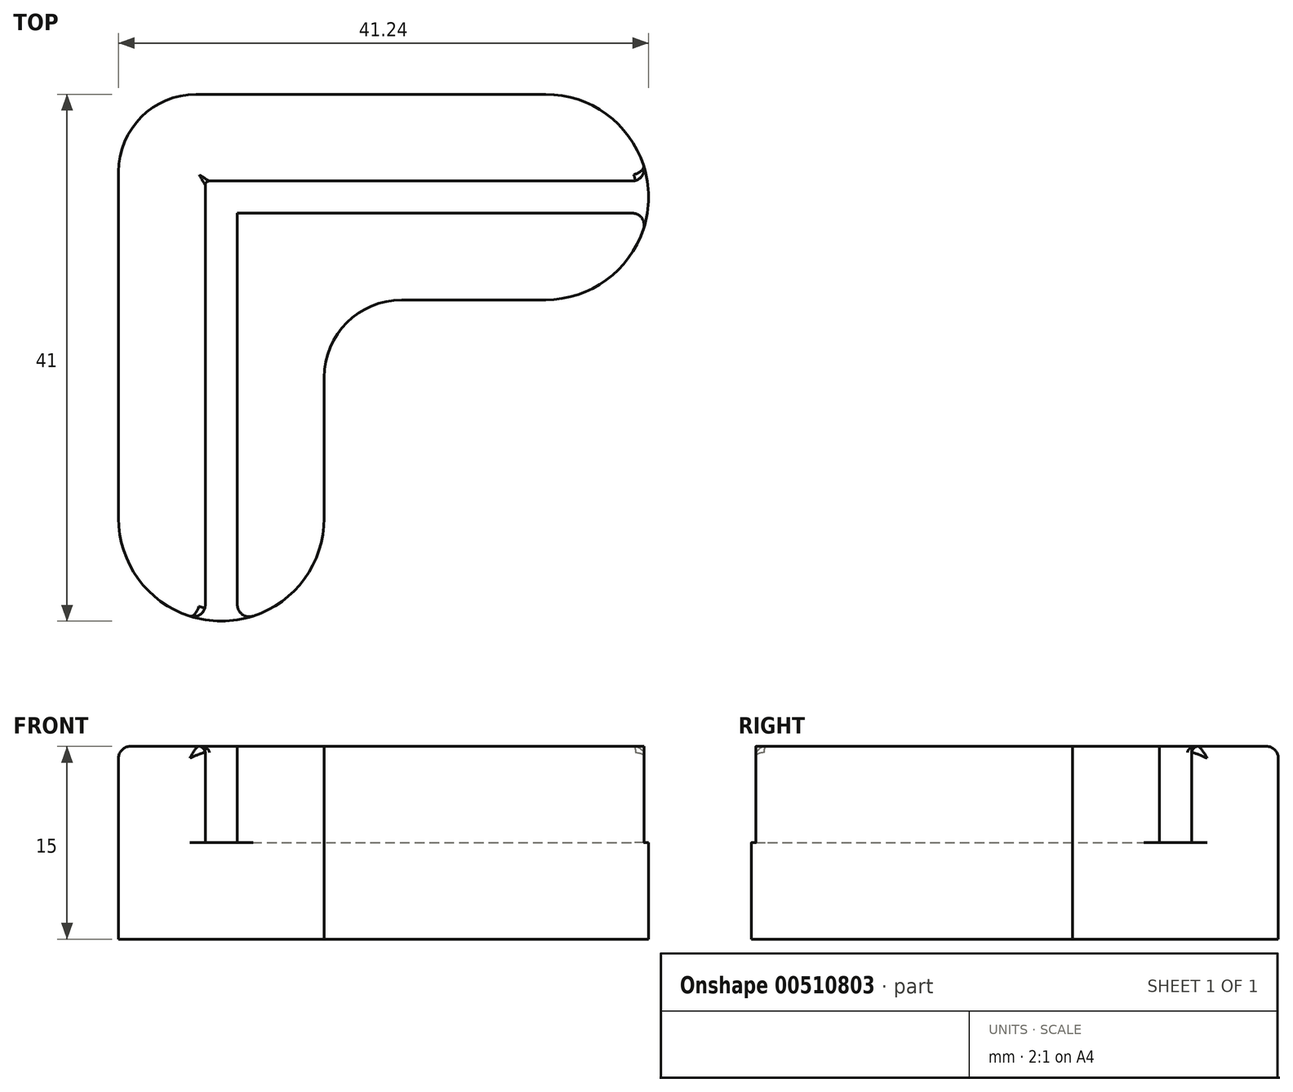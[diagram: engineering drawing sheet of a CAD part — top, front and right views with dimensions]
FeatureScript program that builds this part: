
annotation { "Feature Type Name" : "Feature", "Feature Type Description" : "" }
export const myFeature = defineFeature(function(context is Context, id is Id, definition is map)
    precondition{}
    {
        {
            var Q0;
            Q0=qCreatedBy(makeId("Top.planeOp"),FACE);
            var sketch = newSketch(context, id + "F0", { "sketchPlane" : qUnion([Q0])});
            skCircle(sketch, "E0", {"center": v(-25.24, -25) * mm, "radius": 8 * mm});
            skCircle(sketch, "E1", {"center": v(0, 0) * mm, "radius": 8 * mm});
            skLineSegment(sketch, "E2", {"start": v(0, -8) * mm, "end": v(-17.24, -8) * mm});
            skLineSegment(sketch, "E3", {"start": v(-17.24, -8) * mm, "end": v(-17.24, -25) * mm});
            skLineSegment(sketch, "E4", {"start": v(-33.24, -25) * mm, "end": v(-33.24, 0) * mm});
            skLineSegment(sketch, "E5", {"start": v(0, 8) * mm, "end": v(-33.24, 8) * mm});
            skLineSegment(sketch, "E6", {"start": v(-33.24, 8) * mm, "end": v(-33.24, 0) * mm});
            skSolve(sketch);
        }
        {
            var Q0;
            Q0 = qSketchRegion(id + "F0", true);
            extrude(context, id + "F1", {"entities" : qUnion([Q0]), "depth" : 15 * mm});
        }
        {
            var Q0;
            Q0=makeQuery(id+"F1.opExtrude","CAP_FACE",FACE,{"disambiguationData":[OSD([sQuery(id+"F0.wireOp",EDGE,"E0"),sQuery(id+"F0.wireOp",EDGE,"E1"),sQuery(id+"F0.wireOp",EDGE,"E2"),sQuery(id+"F0.wireOp",EDGE,"E3"),sQuery(id+"F0.wireOp",EDGE,"E4"),sQuery(id+"F0.wireOp",EDGE,"E5"),sQuery(id+"F0.wireOp",EDGE,"E6")])],"isStart":false});
            var sketch = newSketch(context, id + "F2", { "sketchPlane" : qUnion([Q0])});
            skLineSegment(sketch, "E7", {"start": v(9.36, 1.25) * mm, "end": v(9.36, -1.25) * mm});
            skLineSegment(sketch, "E8", {"start": v(-25.24, 1.25) * mm, "end": v(9.36, 1.25) * mm});
            skLineSegment(sketch, "E9", {"start": v(-25.24, -33) * mm, "end": v(-26.49, -33) * mm});
            skLineSegment(sketch, "E10", {"start": v(-25.24, -33) * mm, "end": v(-23.99, -33) * mm});
            skLineSegment(sketch, "E11", {"start": v(-23.99, -33) * mm, "end": v(-23.99, -1.25) * mm});
            skLineSegment(sketch, "E12", {"start": v(-26.49, -33) * mm, "end": v(-26.49, 1.25) * mm});
            skLineSegment(sketch, "E13", {"start": v(-26.49, 1.25) * mm, "end": v(-25.24, 1.25) * mm});
            skLineSegment(sketch, "E14", {"start": v(-23.99, -1.25) * mm, "end": v(9.36, -1.25) * mm});
            skSolve(sketch);
        }
        {
            var Q0;
            Q0 = qSketchRegion(id + "F2", true);
            extrude(context, id + "F3", {"entities" : qUnion([Q0]), "operationType" : NewBodyOperationType.REMOVE, "oppositeDirection" : true, "depth" : (15 / 2) * mm});
        }
        {
            var Q0;
            Q0=makeQuery(id+"F1.opExtrude","SWEPT_EDGE",EDGE,{"disambiguationData":[OSD([sQuery(id+"F0.wireOp",EDGE,"E2"),sQuery(id+"F0.wireOp",EDGE,"E3")])]});
            var Q1;
            Q1=makeQuery(id+"F1.opExtrude","SWEPT_EDGE",EDGE,{"disambiguationData":[OSD([sQuery(id+"F0.wireOp",EDGE,"E5"),sQuery(id+"F0.wireOp",EDGE,"E6")])]});
            fillet(context, id + "F4", {"entities" : qUnion([Q0, Q1]), "radius" : 6.04 * mm, "tangentPropagation" : true, "allowEdgeOverflow" : false});
        }
        {
            var Q0;
            Q0=makeQuery(id+"F3.boolean.opBoolean","COPY",EDGE,{"derivedFrom":makeQuery(id+"F3.opExtrude","CAP_EDGE",EDGE,{"disambiguationData":[OSD([sQuery(id+"F2.wireOp",EDGE,"E8"),sQuery(id+"F2.wireOp",EDGE,"E13")])],"isStart":true})});
            var Q1;
            Q1=makeQuery(id+"F3.boolean.opBoolean","COPY",EDGE,{"derivedFrom":makeQuery(id+"F3.opExtrude","CAP_EDGE",EDGE,{"disambiguationData":[OSD([sQuery(id+"F2.wireOp",EDGE,"E14")])],"isStart":true})});
            var Q2;
            Q2=makeQuery(id+"F3.boolean.opBoolean","COPY",EDGE,{"derivedFrom":makeQuery(id+"F3.opExtrude","CAP_EDGE",EDGE,{"disambiguationData":[OSD([sQuery(id+"F2.wireOp",EDGE,"E12")])],"isStart":true})});
            var Q3;
            Q3=makeQuery(id+"F3.boolean.opBoolean","COPY",EDGE,{"derivedFrom":makeQuery(id+"F3.opExtrude","CAP_EDGE",EDGE,{"disambiguationData":[OSD([sQuery(id+"F2.wireOp",EDGE,"E11")])],"isStart":true})});
            fillet(context, id + "F5", {"entities" : qUnion([Q0, Q1, Q2, Q3]), "radius" : 0.48 * mm, "tangentPropagation" : true, "allowEdgeOverflow" : false});
        }
        {
            var Q0;
            Q0=makeQuery(id+"F5.opFillet","BLEND_EDGE",EDGE,{"blendedFrom":[makeQuery(id+"F3.boolean.opBoolean","COPY",EDGE,{"derivedFrom":makeQuery(id+"F3.opExtrude","CAP_EDGE",EDGE,{"disambiguationData":[OSD([sQuery(id+"F2.wireOp",EDGE,"E8"),sQuery(id+"F2.wireOp",EDGE,"E13")])],"isStart":true})}),makeQuery(id+"F3.boolean.opBoolean","COPY",EDGE,{"derivedFrom":makeQuery(id+"F3.opExtrude","CAP_EDGE",EDGE,{"disambiguationData":[OSD([sQuery(id+"F2.wireOp",EDGE,"E12")])],"isStart":true})})],"blendedInto":[]});
            var Q1;
            Q1=makeQuery(id+"F5.opFillet","BLEND_EDGE",EDGE,{"blendedFrom":[makeQuery(id+"F3.boolean.opBoolean","COPY",EDGE,{"derivedFrom":makeQuery(id+"F3.opExtrude","CAP_EDGE",EDGE,{"disambiguationData":[OSD([sQuery(id+"F2.wireOp",EDGE,"E11")])],"isStart":true})}),makeQuery(id+"F3.boolean.opBoolean","COPY",EDGE,{"derivedFrom":makeQuery(id+"F3.opExtrude","CAP_EDGE",EDGE,{"disambiguationData":[OSD([sQuery(id+"F2.wireOp",EDGE,"E14")])],"isStart":true})})],"blendedInto":[]});
            fillet(context, id + "F6", {"entities" : qUnion([Q0, Q1]), "radius" : 0.32 * mm, "tangentPropagation" : true, "allowEdgeOverflow" : false});
        }
        {
            var Q0;
            Q0=makeQuery(id+"F3.boolean.opBoolean","INTERSECT",EDGE,{"derivedFrom":[makeQuery(id+"F1.opExtrude","SWEPT_FACE",FACE,{"disambiguationData":[OSD([sQuery(id+"F0.wireOp",EDGE,"E0")])]}),makeQuery(id+"F3.opExtrude","SWEPT_FACE",FACE,{"disambiguationData":[OSD([sQuery(id+"F2.wireOp",EDGE,"E12")])]})]});
            var Q1;
            Q1=makeQuery(id+"F3.boolean.opBoolean","INTERSECT",EDGE,{"derivedFrom":[makeQuery(id+"F1.opExtrude","SWEPT_FACE",FACE,{"disambiguationData":[OSD([sQuery(id+"F0.wireOp",EDGE,"E0")])]}),makeQuery(id+"F3.opExtrude","SWEPT_FACE",FACE,{"disambiguationData":[OSD([sQuery(id+"F2.wireOp",EDGE,"E11")])]})]});
            var Q2;
            Q2=makeQuery(id+"F3.boolean.opBoolean","INTERSECT",EDGE,{"derivedFrom":[makeQuery(id+"F1.opExtrude","SWEPT_FACE",FACE,{"disambiguationData":[OSD([sQuery(id+"F0.wireOp",EDGE,"E1")])]}),makeQuery(id+"F3.opExtrude","SWEPT_FACE",FACE,{"disambiguationData":[OSD([sQuery(id+"F2.wireOp",EDGE,"E14")])]})]});
            var Q3;
            Q3=makeQuery(id+"F3.boolean.opBoolean","INTERSECT",EDGE,{"derivedFrom":[makeQuery(id+"F1.opExtrude","SWEPT_FACE",FACE,{"disambiguationData":[OSD([sQuery(id+"F0.wireOp",EDGE,"E1")])]}),makeQuery(id+"F3.opExtrude","SWEPT_FACE",FACE,{"disambiguationData":[OSD([sQuery(id+"F2.wireOp",EDGE,"E8"),sQuery(id+"F2.wireOp",EDGE,"E13")])]})]});
            fillet(context, id + "F7", {"entities" : qUnion([Q0, Q1, Q2, Q3]), "radius" : 0.93 * mm, "tangentPropagation" : true, "allowEdgeOverflow" : false});
        }
    });
